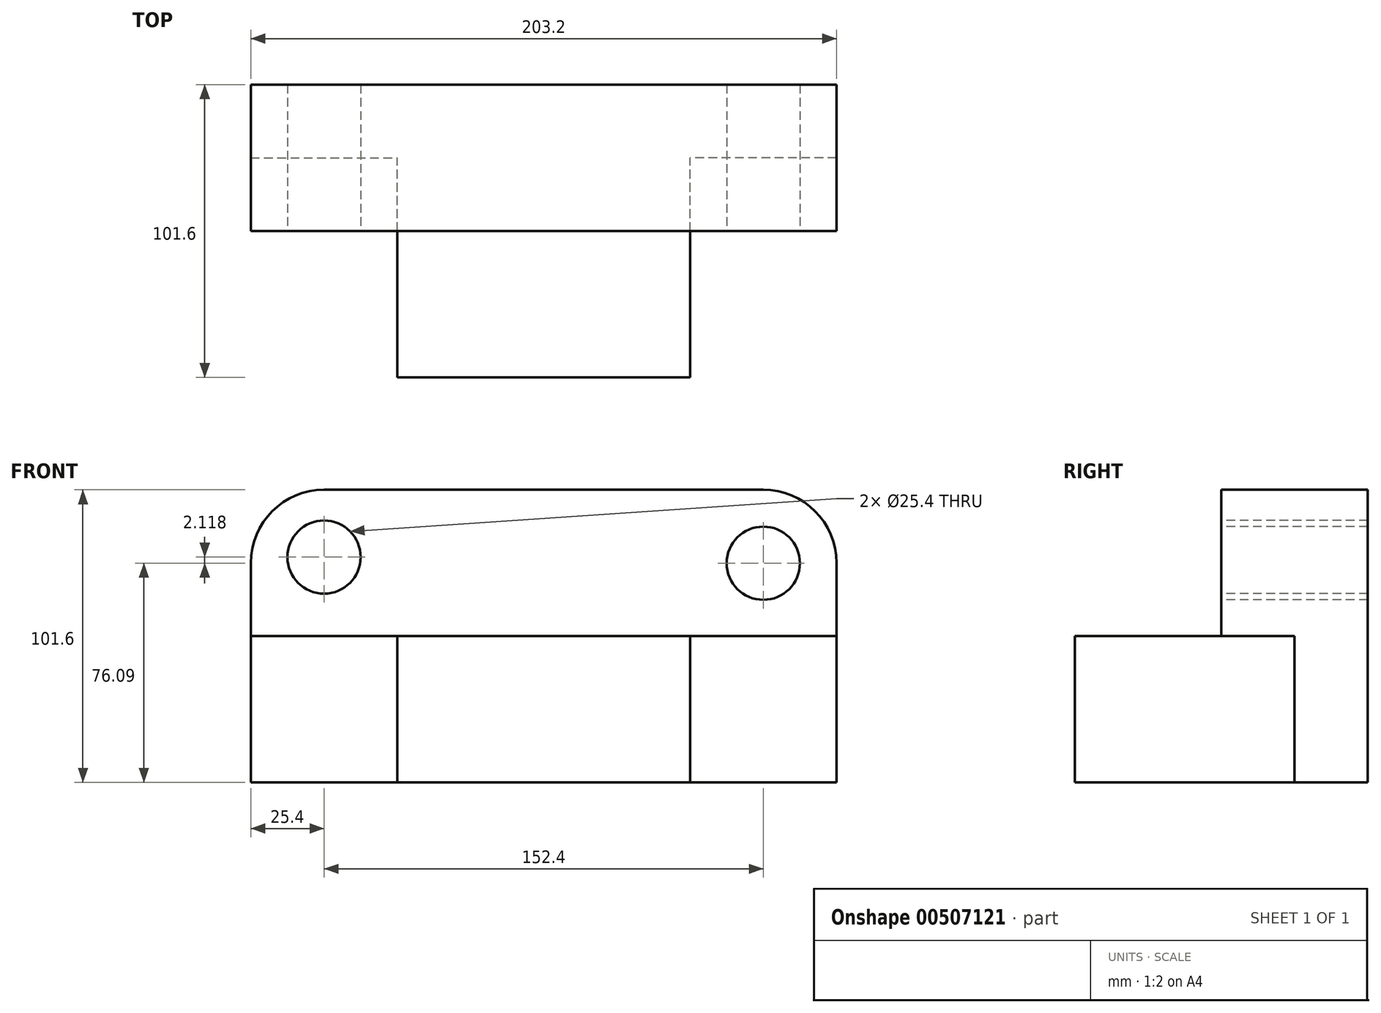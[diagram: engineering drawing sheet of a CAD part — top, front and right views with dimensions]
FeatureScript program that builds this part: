
annotation { "Feature Type Name" : "Feature", "Feature Type Description" : "" }
export const myFeature = defineFeature(function(context is Context, id is Id, definition is map)
    precondition{}
    {
        {
            var Q0;
            Q0=qCreatedBy(makeId("Top.planeOp"),FACE);
            var sketch = newSketch(context, id + "F0", { "sketchPlane" : qUnion([Q0])});
            skLineSegment(sketch, "E0.bottom", {"start": v(101.6, 50.8) * mm, "end": v(-101.6, 50.8) * mm});
            skLineSegment(sketch, "E0.top", {"start": v(101.6, -50.8) * mm, "end": v(-101.6, -50.8) * mm});
            skLineSegment(sketch, "E0.left", {"start": v(101.6, 50.8) * mm, "end": v(101.6, -50.8) * mm});
            skLineSegment(sketch, "E0.right", {"start": v(-101.6, 50.8) * mm, "end": v(-101.6, -50.8) * mm});
            skPoint(sketch, "E0.middle", {"position": v(0, 0) * mm});
            skSolve(sketch);
        }
        {
            var Q0;
            Q0 = qSketchRegion(id + "F0", true);
            extrude(context, id + "F1", {"entities" : qUnion([Q0]), "depth" : 101.6 * mm});
        }
        {
            var Q0;
            Q0=makeQuery(id+"F1.opExtrude","CAP_FACE",FACE,{"disambiguationData":[OSD([sQuery(id+"F0.wireOp",EDGE,"E0.bottom"),sQuery(id+"F0.wireOp",EDGE,"E0.top"),sQuery(id+"F0.wireOp",EDGE,"E0.left"),sQuery(id+"F0.wireOp",EDGE,"E0.right")])],"isStart":false});
            var sketch = newSketch(context, id + "F2", { "sketchPlane" : qUnion([Q0])});
            skLineSegment(sketch, "E1.bottom", {"start": v(101.6, -50.8) * mm, "end": v(-101.6, -50.8) * mm});
            skLineSegment(sketch, "E1.top", {"start": v(101.6, 0) * mm, "end": v(-101.6, 0) * mm});
            skLineSegment(sketch, "E1.left", {"start": v(101.6, -50.8) * mm, "end": v(101.6, 0) * mm});
            skLineSegment(sketch, "E1.right", {"start": v(-101.6, -50.8) * mm, "end": v(-101.6, 0) * mm});
            skSolve(sketch);
        }
        {
            var Q0;
            Q0 = qSketchRegion(id + "F2", true);
            extrude(context, id + "F3", {"entities" : qUnion([Q0]), "operationType" : NewBodyOperationType.REMOVE, "oppositeDirection" : true, "depth" : 50.8 * mm});
        }
        {
            var Q0;
            Q0=makeQuery(id+"F1.opExtrude","CAP_FACE",FACE,{"disambiguationData":[OSD([sQuery(id+"F0.wireOp",EDGE,"E0.bottom"),sQuery(id+"F0.wireOp",EDGE,"E0.top"),sQuery(id+"F0.wireOp",EDGE,"E0.left"),sQuery(id+"F0.wireOp",EDGE,"E0.right")])],"isStart":true});
            var sketch = newSketch(context, id + "F4", { "sketchPlane" : qUnion([Q0])});
            skLineSegment(sketch, "E2.bottom", {"start": v(101.6, 50.8) * mm, "end": v(50.8, 50.8) * mm});
            skLineSegment(sketch, "E2.top", {"start": v(101.6, -25.4) * mm, "end": v(50.8, -25.4) * mm});
            skLineSegment(sketch, "E2.left", {"start": v(101.6, 50.8) * mm, "end": v(101.6, -25.4) * mm});
            skLineSegment(sketch, "E2.right", {"start": v(50.8, 50.8) * mm, "end": v(50.8, -25.4) * mm});
            skSolve(sketch);
        }
        {
            var Q0;
            Q0 = qSketchRegion(id + "F4", true);
            extrude(context, id + "F5", {"entities" : qUnion([Q0]), "operationType" : NewBodyOperationType.REMOVE, "oppositeDirection" : true, "depth" : 50.8 * mm});
        }
        {
            var Q0;
            Q0=makeQuery(id+"F1.opExtrude","CAP_FACE",FACE,{"disambiguationData":[OSD([sQuery(id+"F0.wireOp",EDGE,"E0.bottom"),sQuery(id+"F0.wireOp",EDGE,"E0.top"),sQuery(id+"F0.wireOp",EDGE,"E0.left"),sQuery(id+"F0.wireOp",EDGE,"E0.right")])],"isStart":true});
            var sketch = newSketch(context, id + "F6", { "sketchPlane" : qUnion([Q0])});
            skLineSegment(sketch, "E3.bottom", {"start": v(-101.6, 50.8) * mm, "end": v(-50.8, 50.8) * mm});
            skLineSegment(sketch, "E3.top", {"start": v(-101.6, -25.4) * mm, "end": v(-50.8, -25.4) * mm});
            skLineSegment(sketch, "E3.left", {"start": v(-101.6, 50.8) * mm, "end": v(-101.6, -25.4) * mm});
            skLineSegment(sketch, "E3.right", {"start": v(-50.8, 50.8) * mm, "end": v(-50.8, -25.4) * mm});
            skSolve(sketch);
        }
        {
            var Q0;
            Q0 = qSketchRegion(id + "F6", true);
            extrude(context, id + "F7", {"entities" : qUnion([Q0]), "operationType" : NewBodyOperationType.REMOVE, "oppositeDirection" : true, "depth" : 50.8 * mm});
        }
        {
            var Q0;
            Q0=makeQuery(id+"F3.boolean.opBoolean","COPY",FACE,{"derivedFrom":makeQuery(id+"F3.opExtrude","SWEPT_FACE",FACE,{"disambiguationData":[OSD([sQuery(id+"F2.wireOp",EDGE,"E1.top")])]})});
            var sketch = newSketch(context, id + "F8", { "sketchPlane" : qUnion([Q0])});
            skCircle(sketch, "E4", {"center": v(-76.2, 78.2) * mm, "radius": 12.7 * mm});
            skSolve(sketch);
        }
        {
            var Q0;
            Q0 = qSketchRegion(id + "F8", true);
            var Q1;
            Q1=makeQuery(id+"F1.opExtrude","SWEPT_FACE",FACE,{"disambiguationData":[OSD([sQuery(id+"F0.wireOp",EDGE,"E0.bottom")])]});
            extrude(context, id + "F9", {"entities" : qUnion([Q0]), "operationType" : NewBodyOperationType.REMOVE, "endBound" : BoundingType.UP_TO_SURFACE, "oppositeDirection" : true, "endBoundEntityFace" : qUnion([Q1]), "depth" : 50.8 * mm});
        }
        {
            var Q0;
            Q0=makeQuery(id+"F1.opExtrude","CAP_EDGE",EDGE,{"disambiguationData":[OSD([sQuery(id+"F0.wireOp",EDGE,"E0.right")])],"isStart":false});
            fillet(context, id + "F10", {"entities" : qUnion([Q0]), "radius" : 25.4 * mm, "tangentPropagation" : true, "allowEdgeOverflow" : false});
        }
        {
            var Q0;
            Q0=makeQuery(id+"F3.boolean.opBoolean","COPY",FACE,{"derivedFrom":makeQuery(id+"F3.opExtrude","SWEPT_FACE",FACE,{"disambiguationData":[OSD([sQuery(id+"F2.wireOp",EDGE,"E1.top")])]})});
            var sketch = newSketch(context, id + "F11", { "sketchPlane" : qUnion([Q0])});
            skCircle(sketch, "E5", {"center": v(76.2, 76.09) * mm, "radius": 12.7 * mm});
            skSolve(sketch);
        }
        {
            var Q0;
            Q0 = qSketchRegion(id + "F11", true);
            var Q1;
            Q1=makeQuery(id+"F1.opExtrude","SWEPT_FACE",FACE,{"disambiguationData":[OSD([sQuery(id+"F0.wireOp",EDGE,"E0.bottom")])]});
            extrude(context, id + "F12", {"entities" : qUnion([Q0]), "operationType" : NewBodyOperationType.REMOVE, "endBound" : BoundingType.UP_TO_SURFACE, "oppositeDirection" : true, "endBoundEntityFace" : qUnion([Q1]), "depth" : 25.4 * mm});
        }
        {
            var Q0;
            Q0=makeQuery(id+"F1.opExtrude","CAP_EDGE",EDGE,{"disambiguationData":[OSD([sQuery(id+"F0.wireOp",EDGE,"E0.left")])],"isStart":false});
            fillet(context, id + "F13", {"entities" : qUnion([Q0]), "radius" : 25.4 * mm, "tangentPropagation" : true, "allowEdgeOverflow" : false});
        }
    });
